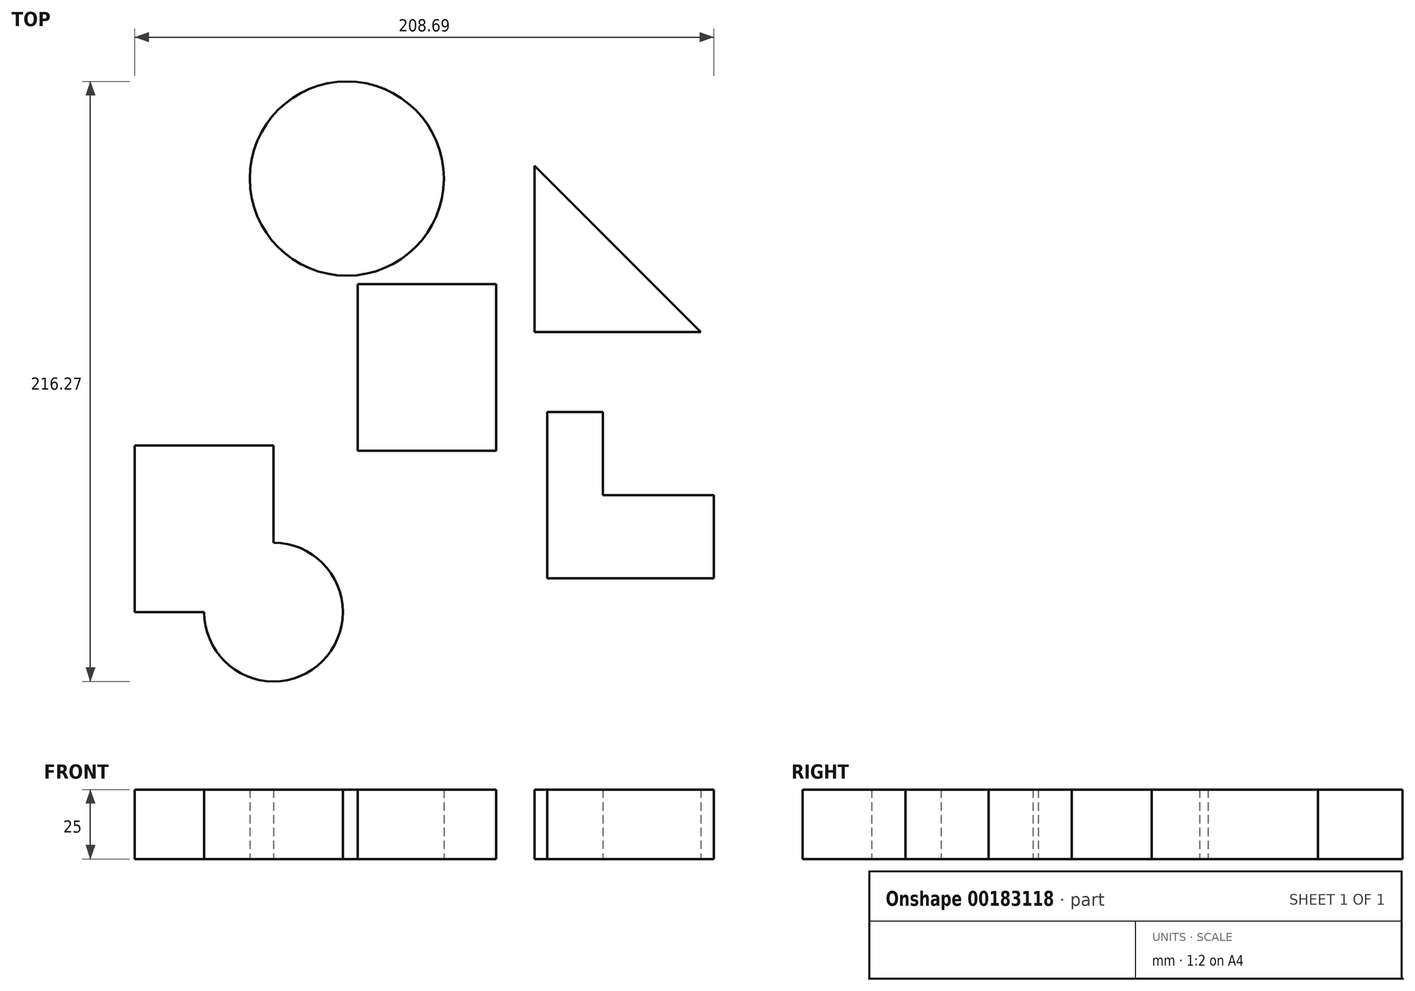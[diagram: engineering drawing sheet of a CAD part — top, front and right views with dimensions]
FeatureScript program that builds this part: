
annotation { "Feature Type Name" : "Feature", "Feature Type Description" : "" }
export const myFeature = defineFeature(function(context is Context, id is Id, definition is map)
    precondition{}
    {
        {
            var Q0;
            Q0=qCreatedBy(makeId("Top.planeOp"),FACE);
            var sketch = newSketch(context, id + "F0", { "sketchPlane" : qUnion([Q0])});
            skLineSegment(sketch, "E0.bottom", {"start": v(-44.68, 29.77) * mm, "end": v(5.32, 29.77) * mm});
            skLineSegment(sketch, "E0.top", {"start": v(-44.68, -30.23) * mm, "end": v(5.32, -30.23) * mm});
            skLineSegment(sketch, "E0.left", {"start": v(-44.68, 29.77) * mm, "end": v(-44.68, -30.23) * mm});
            skLineSegment(sketch, "E0.right", {"start": v(5.32, 29.77) * mm, "end": v(5.32, -30.23) * mm});
            skSolve(sketch);
        }
        {
            var Q0;
            Q0=qCreatedBy(makeId("Top.planeOp"),FACE);
            var sketch = newSketch(context, id + "F1", { "sketchPlane" : qUnion([Q0])});
            skLineSegment(sketch, "E1", {"start": v(19.06, 72.5) * mm, "end": v(19.06, 12.5) * mm});
            skLineSegment(sketch, "E2", {"start": v(19.06, 12.5) * mm, "end": v(79.06, 12.5) * mm});
            skLineSegment(sketch, "E3", {"start": v(19.06, 72.5) * mm, "end": v(79.06, 12.5) * mm});
            skCircle(sketch, "E4", {"center": v(-48.57, 67.87) * mm, "radius": 35 * mm});
            skLineSegment(sketch, "E5.bottom", {"start": v(43.7, -46.29) * mm, "end": v(83.7, -46.29) * mm});
            skLineSegment(sketch, "E5.top", {"start": v(23.7, -76.29) * mm, "end": v(83.7, -76.29) * mm});
            skLineSegment(sketch, "E5.left", {"start": v(23.7, -46.29) * mm, "end": v(23.7, -76.29) * mm});
            skLineSegment(sketch, "E5.right", {"start": v(83.7, -46.29) * mm, "end": v(83.7, -76.29) * mm});
            skLineSegment(sketch, "E6.bottom", {"start": v(23.7, -76.29) * mm, "end": v(43.7, -76.29) * mm});
            skLineSegment(sketch, "E6.top", {"start": v(23.7, -16.29) * mm, "end": v(43.7, -16.29) * mm});
            skLineSegment(sketch, "E6.left", {"start": v(23.7, -76.29) * mm, "end": v(23.7, -16.29) * mm});
            skLineSegment(sketch, "E6.right", {"start": v(43.7, -46.29) * mm, "end": v(43.7, -16.29) * mm});
            skLineSegment(sketch, "E7.bottom", {"start": v(-125, -28.4) * mm, "end": v(-75, -28.4) * mm});
            skLineSegment(sketch, "E7.top", {"start": v(-125, -88.4) * mm, "end": v(-100, -88.4) * mm});
            skLineSegment(sketch, "E7.left", {"start": v(-125, -28.4) * mm, "end": v(-125, -88.4) * mm});
            skLineSegment(sketch, "E7.right", {"start": v(-75, -28.4) * mm, "end": v(-75, -63.4) * mm});
            skArc(sketch, "E8", {"start": v(-100, -88.4) * mm, "mid": v(-57.31, -106.08) * mm, "end": v(-75, -63.4) * mm});
            skSolve(sketch);
        }
        {
            var Q0;
            Q0=makeQuery(id+"F1.imprint","IMPRINT",FACE,{"disambiguationData":[TD([[makeQuery(id+"F1.imprint","IMPRINT",EDGE,{"derivedFrom":sQuery(id+"F1.wireOp",EDGE,"E4")}),1.0]])]});
            extrude(context, id + "F2", {"entities" : qUnion([Q0]), "depth" : 25 * mm});
        }
        {
            var Q0;
            Q0=makeQuery(id+"F0.imprint","IMPRINT",FACE,{"disambiguationData":[TD([[makeQuery(id+"F0.imprint","IMPRINT",EDGE,{"derivedFrom":sQuery(id+"F0.wireOp",EDGE,"E0.bottom")}),-1.0]])]});
            extrude(context, id + "F3", {"entities" : qUnion([Q0]), "depth" : 25 * mm});
        }
        {
            var Q0;
            Q0 = qSketchRegion(id + "F1", true);
            extrude(context, id + "F4", {"entities" : qUnion([Q0]), "operationType" : NewBodyOperationType.ADD, "depth" : 25 * mm});
        }
    });
